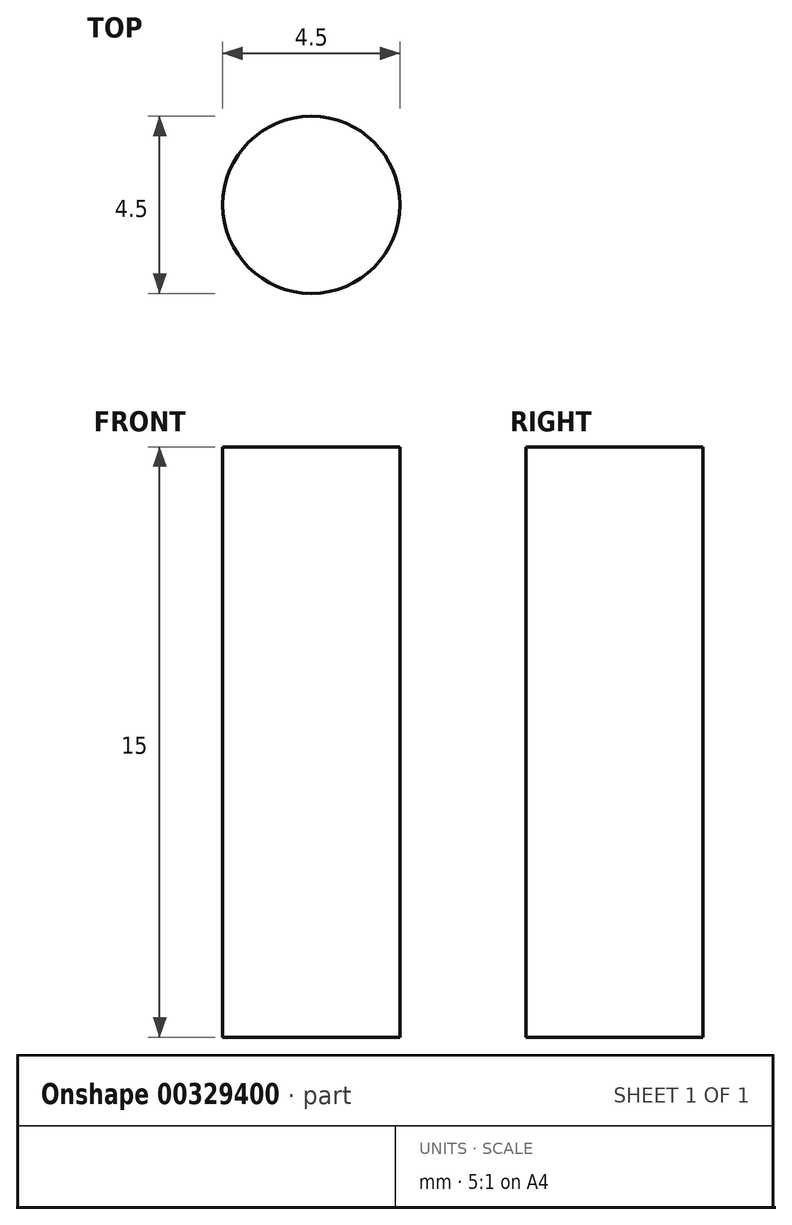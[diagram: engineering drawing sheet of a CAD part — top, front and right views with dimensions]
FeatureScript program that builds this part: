
annotation { "Feature Type Name" : "Feature", "Feature Type Description" : "" }
export const myFeature = defineFeature(function(context is Context, id is Id, definition is map)
    precondition{}
    {
        {
            var Q0;
            Q0=qCreatedBy(makeId("Top.planeOp"),FACE);
            var sketch = newSketch(context, id + "F0", { "sketchPlane" : qUnion([Q0])});
            skCircle(sketch, "E0", {"center": v(0, 0) * mm, "radius": 2.25 * mm});
            skSolve(sketch);
        }
        {
            var Q0;
            Q0=makeQuery(id+"F0.imprint","IMPRINT",FACE,{"disambiguationData":[TD([[makeQuery(id+"F0.imprint","IMPRINT",EDGE,{"derivedFrom":sQuery(id+"F0.wireOp",EDGE,"E0")}),1.0]])]});
            extrude(context, id + "F1", {"entities" : qUnion([Q0]), "depth" : 15 * mm});
        }
    });
